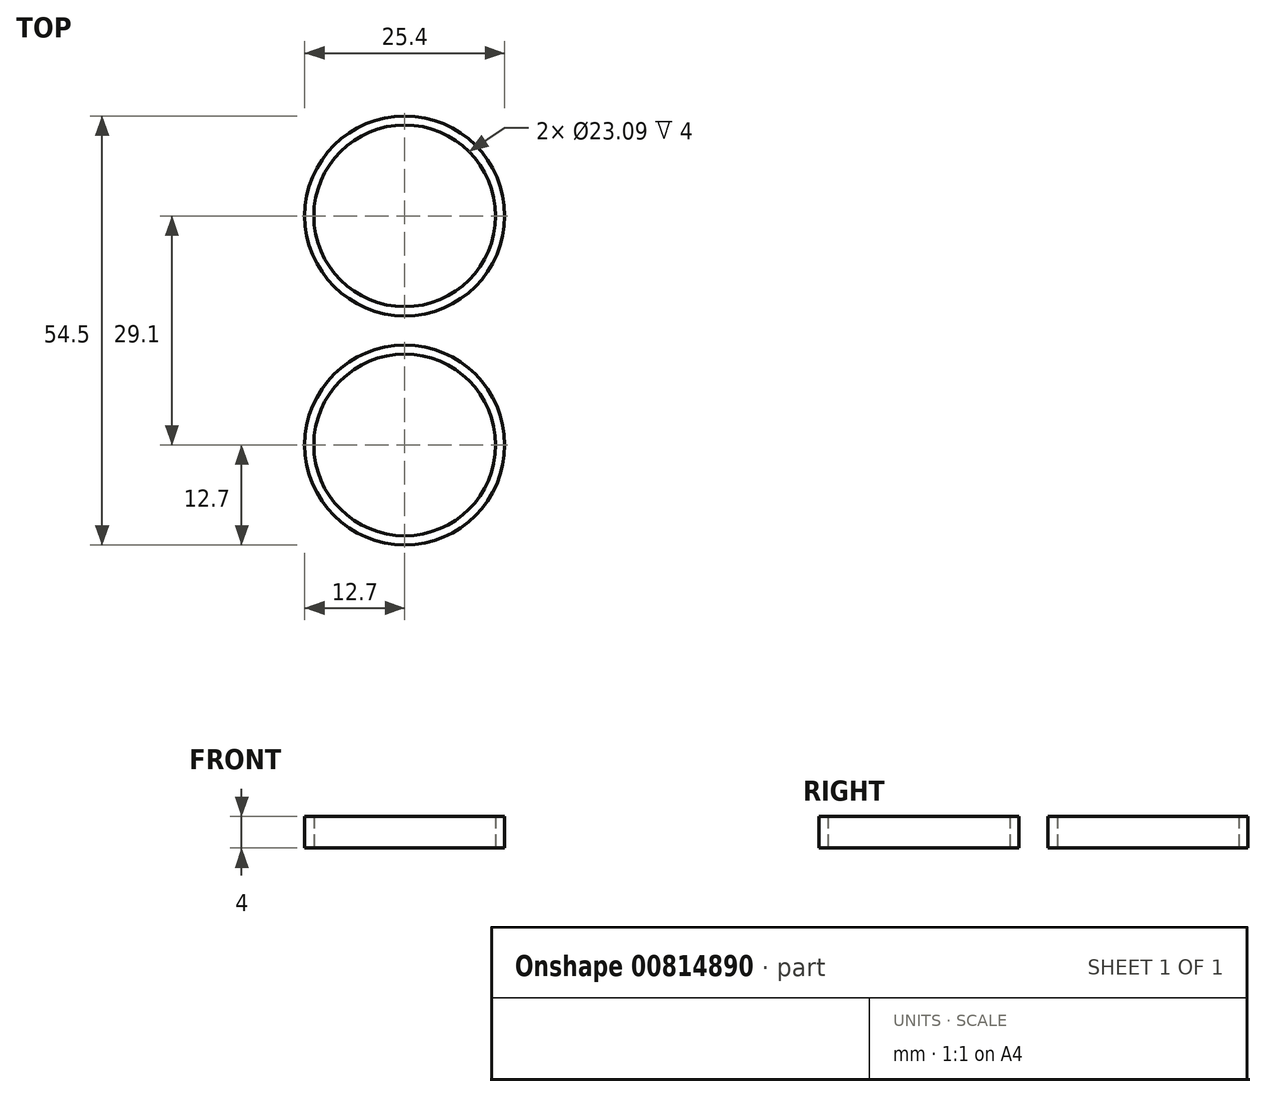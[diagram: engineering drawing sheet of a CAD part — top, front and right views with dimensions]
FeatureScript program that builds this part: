
annotation { "Feature Type Name" : "Feature", "Feature Type Description" : "" }
export const myFeature = defineFeature(function(context is Context, id is Id, definition is map)
    precondition{}
    {
        {
            var Q0;
            Q0=qCreatedBy(makeId("Top.planeOp"),FACE);
            var sketch = newSketch(context, id + "F0", { "sketchPlane" : qUnion([Q0])});
            skCircle(sketch, "E0", {"center": v(0, 0) * mm, "radius": 12.7 * mm});
            skCircle(sketch, "E1", {"center": v(0, 0) * mm, "radius": 11.55 * mm});
            skSolve(sketch);
        }
        {
            var Q0;
            Q0=makeQuery(id+"F0.imprint","IMPRINT",FACE,{"disambiguationData":[TD([[makeQuery(id+"F0.imprint","IMPRINT",EDGE,{"derivedFrom":sQuery(id+"F0.wireOp",EDGE,"E0")}),1.0]])]});
            extrude(context, id + "F1", {"entities" : qUnion([Q0]), "depth" : 4 * mm, "offsetDistance" : 25 * mm});
        }
        {
            var Q0;
            Q0=makeQuery(id+"F1.opExtrude","SWEPT_BODY",BODY,{"disambiguationData":[OSD([sQuery(id+"F0.wireOp",EDGE,"E0"),sQuery(id+"F0.wireOp",EDGE,"E1")])]});
            transform(context, id + "F2", {"entities" : qUnion([Q0]), "transformType" : TransformType.TRANSLATION_3D, "dx" : 0 * mm, "dy" : 29.1 * mm, "dz" : 0 * mm, "makeCopy" : true});
        }
    });
